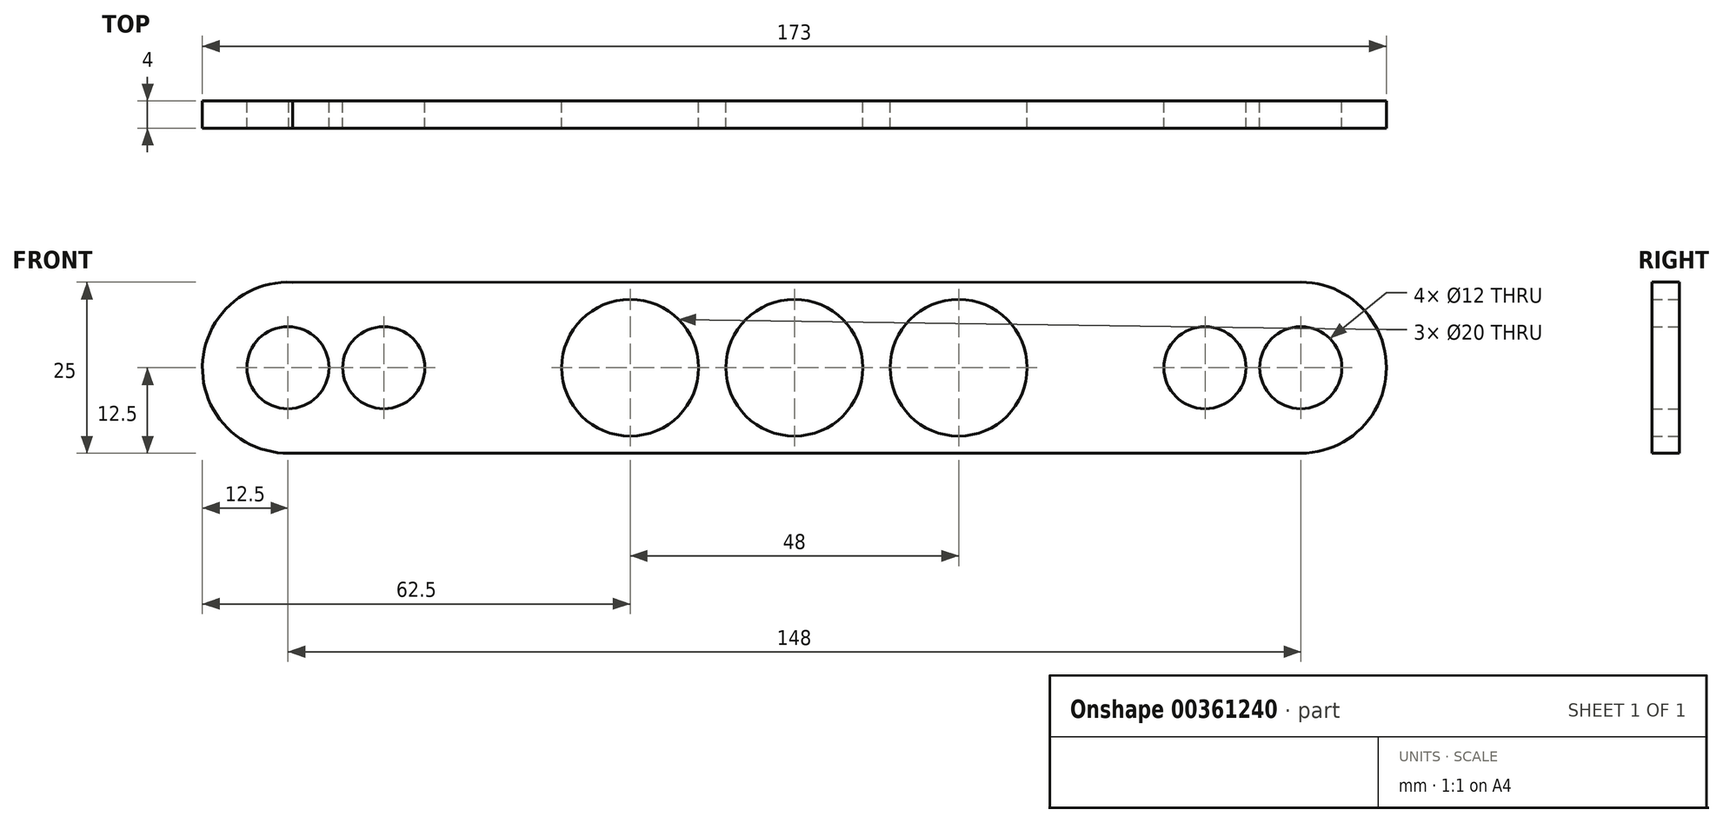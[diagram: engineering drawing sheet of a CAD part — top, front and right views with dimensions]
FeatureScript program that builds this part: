
annotation { "Feature Type Name" : "Feature", "Feature Type Description" : "" }
export const myFeature = defineFeature(function(context is Context, id is Id, definition is map)
    precondition{}
    {
        {
            var Q0;
            Q0=qCreatedBy(makeId("Front.planeOp"),FACE);
            var sketch = newSketch(context, id + "F0", { "sketchPlane" : qUnion([Q0])});
            skCircle(sketch, "E0", {"center": v(0, 0) * mm, "radius": 10 * mm});
            skCircle(sketch, "E1", {"center": v(24, 0) * mm, "radius": 10 * mm});
            skCircle(sketch, "E2", {"center": v(-24, 0) * mm, "radius": 10 * mm});
            skCircle(sketch, "E3", {"center": v(60, 0) * mm, "radius": 6 * mm});
            skCircle(sketch, "E4", {"center": v(74, 0) * mm, "radius": 6 * mm});
            skCircle(sketch, "E5", {"center": v(-60, 0) * mm, "radius": 6 * mm});
            skCircle(sketch, "E6", {"center": v(-74, 0) * mm, "radius": 6 * mm});
            skArc(sketch, "E7", {"start": v(-62.7, 5.36) * mm, "mid": v(-84.6, 6.63) * mm, "end": v(-73.87, -12.5) * mm});
            skArc(sketch, "E8", {"start": v(74, -12.5) * mm, "mid": v(86.5, 0) * mm, "end": v(74, 12.5) * mm});
            skLineSegment(sketch, "E9", {"start": v(-73.87, -12.5) * mm, "end": v(74, -12.5) * mm});
            skLineSegment(sketch, "E10", {"start": v(-73.33, 12.48) * mm, "end": v(74, 12.5) * mm});
            skSolve(sketch);
        }
        {
            var Q0;
            Q0 = qSketchRegion(id + "F0", true);
            extrude(context, id + "F1", {"entities" : qUnion([Q0]), "depth" : 4 * mm});
        }
    });
